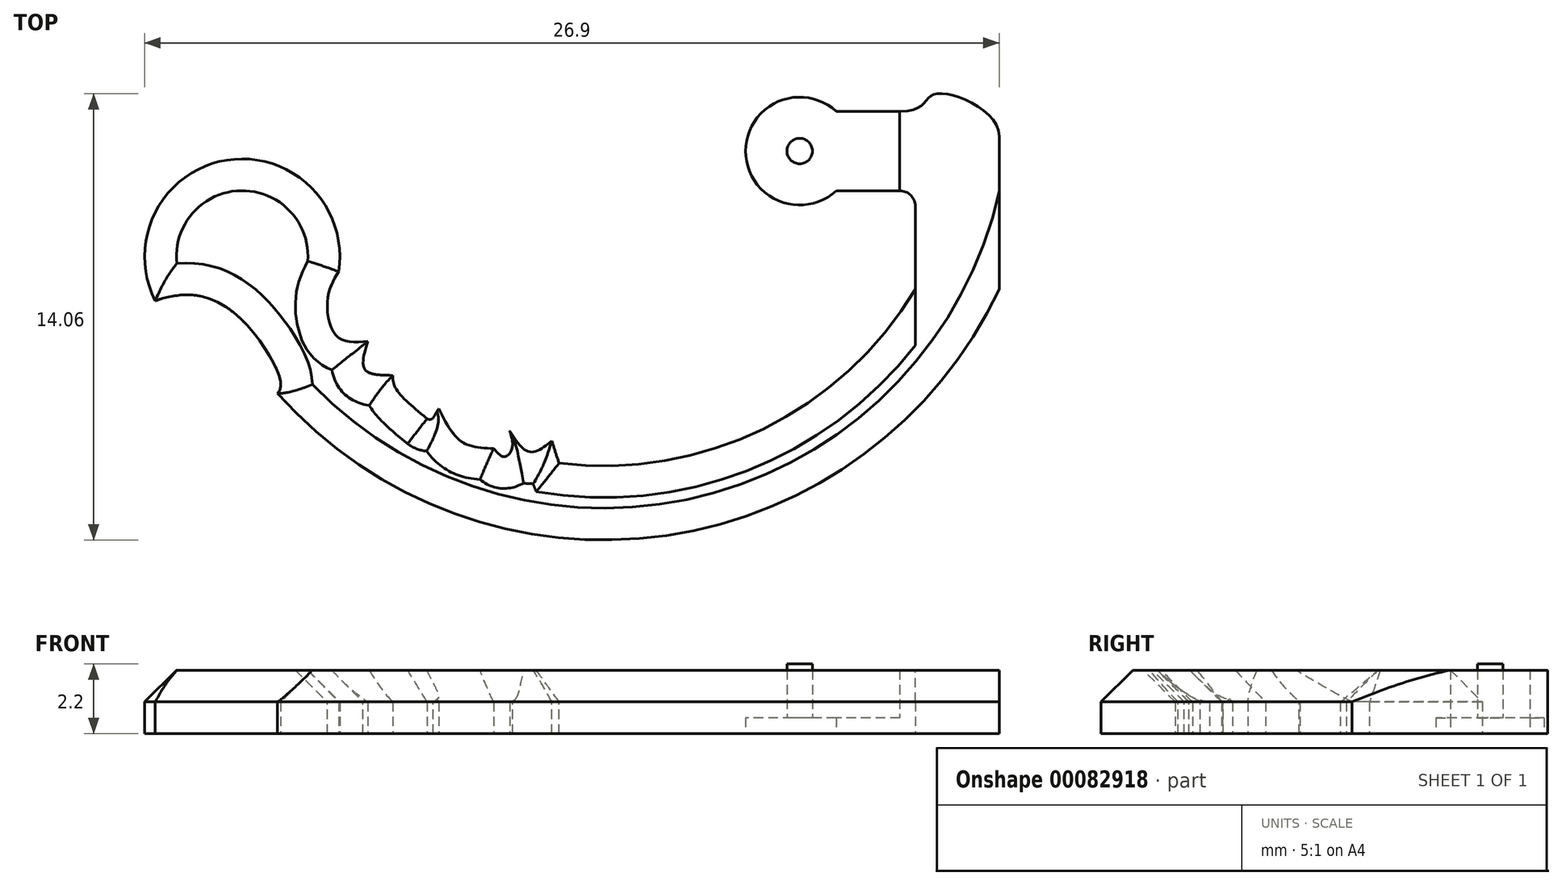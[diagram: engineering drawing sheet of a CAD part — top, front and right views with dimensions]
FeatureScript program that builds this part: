
annotation { "Feature Type Name" : "Feature", "Feature Type Description" : "" }
export const myFeature = defineFeature(function(context is Context, id is Id, definition is map)
    precondition{}
    {
        {
            var Q0;
            Q0=qCreatedBy(makeId("Top.planeOp"),FACE);
            var sketch = newSketch(context, id + "F0", { "sketchPlane" : qUnion([Q0])});
            skLineSegment(sketch, "E0.left", {"start": v(3.15, -1.25) * mm, "end": v(3.15, 1.25) * mm});
            skFitSpline(sketch, "E1", {"points": [v(3.15, 1.25) * mm, v(4.3, 1.8) * mm, v(6.28, 0.46) * mm], "startDerivative": vector(6.12, 0) * mm, "endDerivative": vector(0, -4.23) * mm});
            skLineSegment(sketch, "E2", {"start": v(6.28, 0.46) * mm, "end": v(6.28, -4.35) * mm});
            skArc(sketch, "E3", {"start": v(3.64, -1.74) * mm, "mid": v(3.5, -1.4) * mm, "end": v(3.15, -1.25) * mm});
            skLineSegment(sketch, "E4", {"start": v(3.64, -1.74) * mm, "end": v(3.64, -4.35) * mm});
            skArc(sketch, "E5", {"start": v(-16.44, -7.63) * mm, "mid": v(-4.2, -12.1) * mm, "end": v(6.28, -4.35) * mm});
            skArc(sketch, "E6.0", {"start": v(-17.2, -4.16) * mm, "mid": v(-6.56, -10.9) * mm, "end": v(4.5, -4.86) * mm});
            skFitSpline(sketch, "E7", {"points": [v(-6.56, -10.9) * mm, v(-7.28, -10.36) * mm, v(-7.8, -9.12) * mm], "startDerivative": vector(-1.76, 0.97) * mm, "endDerivative": vector(-0.75, 2.54) * mm});
            skFitSpline(sketch, "E8", {"points": [v(-7.8, -9.12) * mm, v(-8.5, -9.48) * mm, v(-9.12, -8.83) * mm], "startDerivative": vector(-1.5, -1.2) * mm, "endDerivative": vector(-1.15, 1.76) * mm});
            skFitSpline(sketch, "E9", {"points": [v(-9.63, -9.37) * mm, v(-10.63, -9.16) * mm, v(-11.36, -8.1) * mm], "startDerivative": vector(-2.3, 0.09) * mm, "endDerivative": vector(-1.18, 2.4) * mm});
            skFitSpline(sketch, "E10", {"points": [v(-11.36, -8.1) * mm, v(-11.71, -8.86) * mm, v(-11.67, -9.62) * mm], "startDerivative": vector(-0.9, -1.46) * mm, "endDerivative": vector(0.3, -1.56) * mm});
            skFitSpline(sketch, "E11", {"points": [v(-11.6, -8.53) * mm, v(-12.7, -7.48) * mm, v(-12.8, -7.06) * mm], "startDerivative": vector(-2.16, 1.75) * mm, "endDerivative": vector(-0.05, 1.12) * mm});
            skFitSpline(sketch, "E12", {"points": [v(-12.8, -7.06) * mm, v(-13.68, -6.88) * mm, v(-13.59, -5.99) * mm], "startDerivative": vector(-2.23, 0.02) * mm, "endDerivative": vector(0.67, 2.12) * mm});
            skFitSpline(sketch, "E13", {"points": [v(-12.8, -7.06) * mm, v(-13.21, -7.73) * mm, v(-13.45, -8.54) * mm], "startDerivative": vector(-0.91, -1.3) * mm, "endDerivative": vector(-0.36, -1.63) * mm});
            skFitSpline(sketch, "E14", {"points": [v(-13.59, -5.99) * mm, v(-14.56, -5.84) * mm, v(-14.85, -4.62) * mm, v(-14.51, -3.8) * mm], "startDerivative": vector(-3.43, -0.3) * mm, "endDerivative": vector(1.42, 2.32) * mm});
            skFitSpline(sketch, "E15", {"points": [v(-13.59, -5.99) * mm, v(-14.13, -6.91) * mm, v(-14.42, -7.76) * mm], "startDerivative": vector(-1.14, -1.76) * mm, "endDerivative": vector(-0.5, -1.77) * mm});
            skFitSpline(sketch, "E16", {"points": [v(-14.51, -3.8) * mm, v(-15.87, -3.46) * mm, v(-17.2, -4.16) * mm], "startDerivative": vector(-2.8, 1.18) * mm, "endDerivative": vector(-2.59, -1.88) * mm});
            skPoint(sketch, "E17", {"position": v(-16.44, -7.63) * mm});
            skPoint(sketch, "E18.orphan", {"position": v(-18.6, -4.35) * mm});
            skFitSpline(sketch, "E19", {"points": [v(-16.44, -7.63) * mm, v(-16.45, -6.91) * mm, v(-18.22, -4.8) * mm, v(-20.28, -4.71) * mm], "startDerivative": vector(2.1, 1.9) * mm, "endDerivative": vector(-5.6, -1.96) * mm});
            skArc(sketch, "E20", {"start": v(-14.51, -3.8) * mm, "mid": v(-18.03, -0.29) * mm, "end": v(-20.28, -4.71) * mm});
            skPoint(sketch, "E21", {"position": v(-7.57, -9.82) * mm});
            skArc(sketch, "E22.trimOffspring", {"start": v(-7.57, -9.82) * mm, "mid": v(-1.15, -8.75) * mm, "end": v(3.64, -4.35) * mm});
            skArc(sketch, "E23", {"start": v(6.28, -4.35) * mm, "mid": v(4.96, -3.92) * mm, "end": v(3.64, -4.35) * mm});
            skArc(sketch, "E24", {"start": v(6.28, -4.35) * mm, "mid": v(5.35, -4.45) * mm, "end": v(4.5, -4.86) * mm});
            skArc(sketch, "E25", {"start": v(3.64, -4.35) * mm, "mid": v(4.03, -4.67) * mm, "end": v(4.5, -4.86) * mm});
            skArc(sketch, "E26", {"start": v(-11.75, -8.41) * mm, "mid": v(-11.64, -8.45) * mm, "end": v(-11.53, -8.4) * mm});
            skFitSpline(sketch, "E27", {"points": [v(-9.12, -8.83) * mm, v(-9.05, -9.33) * mm, v(-9.28, -9.63) * mm, v(-9.63, -9.37) * mm], "startDerivative": vector(0.47, -1.4) * mm, "endDerivative": vector(-1.1, 1.22) * mm});
            skFitSpline(sketch, "E28", {"points": [v(-9.63, -9.37) * mm, v(-9.8, -9.82) * mm, v(-9.8, -10.37) * mm], "startDerivative": vector(-0.41, -0.9) * mm, "endDerivative": vector(0.08, -1.09) * mm});
            skSolve(sketch);
        }
        {
            var Q0;
            Q0 = qSketchRegion(id + "F0", true);
            extrude(context, id + "F1", {"entities" : qUnion([Q0]), "endBound" : BoundingType.SYMMETRIC, "depth" : 2 * mm});
        }
        {
            var Q0;
            Q0=makeQuery(id+"F1.opExtrude","CAP_EDGE",EDGE,{"disambiguationData":[OSD([sQuery(id+"F0.wireOp",EDGE,"E20")])],"isStart":false});
            var Q1;
            Q1=makeQuery(id+"F1.opExtrude","CAP_EDGE",EDGE,{"disambiguationData":[OSD([sQuery(id+"F0.wireOp",EDGE,"E14")])],"isStart":false});
            var Q2;
            Q2=makeQuery(id+"F1.opExtrude","CAP_EDGE",EDGE,{"disambiguationData":[OSD([sQuery(id+"F0.wireOp",EDGE,"E12")])],"isStart":false});
            var Q3;
            Q3=makeQuery(id+"F1.opExtrude","CAP_EDGE",EDGE,{"disambiguationData":[OSD([sQuery(id+"F0.wireOp",EDGE,"E11")])],"isStart":false});
            var Q4;
            Q4=makeQuery(id+"F1.opExtrude","CAP_EDGE",EDGE,{"disambiguationData":[OSD([sQuery(id+"F0.wireOp",EDGE,"E9")])],"isStart":false});
            var Q5;
            Q5=makeQuery(id+"F1.opExtrude","CAP_EDGE",EDGE,{"disambiguationData":[OSD([sQuery(id+"F0.wireOp",EDGE,"E10")])],"isStart":false});
            var Q6;
            Q6=makeQuery(id+"F1.opExtrude","CAP_EDGE",EDGE,{"disambiguationData":[OSD([sQuery(id+"F0.wireOp",EDGE,"E22.trimOffspring")])],"isStart":false});
            var Q7;
            Q7=makeQuery(id+"F1.opExtrude","CAP_EDGE",EDGE,{"disambiguationData":[OSD([sQuery(id+"F0.wireOp",EDGE,"E7")])],"isStart":false});
            var Q8;
            Q8=makeQuery(id+"F1.opExtrude","CAP_EDGE",EDGE,{"disambiguationData":[OSD([sQuery(id+"F0.wireOp",EDGE,"E26")])],"isStart":false});
            var Q9;
            Q9=makeQuery(id+"F1.opExtrude","CAP_EDGE",EDGE,{"disambiguationData":[OSD([sQuery(id+"F0.wireOp",EDGE,"E27")])],"isStart":false});
            var Q10;
            Q10=makeQuery(id+"F1.opExtrude","CAP_EDGE",EDGE,{"disambiguationData":[OSD([sQuery(id+"F0.wireOp",EDGE,"E8")])],"isStart":false});
            var Q11;
            Q11=makeQuery(id+"F1.opExtrude","CAP_EDGE",EDGE,{"disambiguationData":[OSD([sQuery(id+"F0.wireOp",EDGE,"E5")])],"isStart":false});
            var Q12;
            Q12=makeQuery(id+"F1.opExtrude","CAP_EDGE",EDGE,{"disambiguationData":[OSD([sQuery(id+"F0.wireOp",EDGE,"E19")])],"isStart":false});
            chamfer(context, id + "F2", {"entities" : qUnion([Q0, Q1, Q2, Q3, Q4, Q5, Q6, Q7, Q8, Q9, Q10, Q11, Q12]), "width" : 1 * mm, "tangentPropagation" : true});
        }
        {
            var Q0;
            Q0=qCreatedBy(makeId("Top.planeOp"),FACE);
            var sketch = newSketch(context, id + "F3", { "sketchPlane" : qUnion([Q0])});
            skLineSegment(sketch, "E29.bottom", {"start": v(3.15, 1.25) * mm, "end": v(1.15, 1.25) * mm});
            skLineSegment(sketch, "E29.top", {"start": v(3.15, -1.25) * mm, "end": v(1.15, -1.25) * mm});
            skLineSegment(sketch, "E29.left", {"start": v(3.15, 1.25) * mm, "end": v(3.15, -1.25) * mm});
            skLineSegment(sketch, "E29.right", {"start": v(1.15, 1.25) * mm, "end": v(1.15, -1.25) * mm});
            skCircle(sketch, "E30", {"center": v(0, 0) * mm, "radius": 1.7 * mm});
            skCircle(sketch, "E31", {"center": v(0, 0) * mm, "radius": 0.4 * mm});
            skSolve(sketch);
        }
        {
            var Q0;
            Q0=makeQuery(id+"F3.imprint","IMPRINT",FACE,{"disambiguationData":[TD([[makeQuery(id+"F3.imprint","IMPRINT",EDGE,{"derivedFrom":sQuery(id+"F3.wireOp",EDGE,"E31")}),1.0]])]});
            var Q1;
            {var subQ0=sQuery(id+"F3.wireOp",EDGE,"E29.right");Q1=makeQuery(id+"F3.imprint","IMPRINT",FACE,{"disambiguationData":[TD([[makeQuery(id+"F3.imprint","IMPRINT",EDGE,{"derivedFrom":subQ0}),-1.0]])]});}
            var Q2;
            {var subQ0=sQuery(id+"F3.wireOp",EDGE,"E29.bottom");Q2=makeQuery(id+"F3.imprint","IMPRINT",FACE,{"disambiguationData":[TD([[makeQuery(id+"F3.imprint","IMPRINT",EDGE,{"derivedFrom":subQ0}),1.0]])]});}
            var Q3;
            {var subQ0=sQuery(id+"F3.wireOp",EDGE,"E29.right");Q3=makeQuery(id+"F3.imprint","IMPRINT",FACE,{"disambiguationData":[TD([[makeQuery(id+"F3.imprint","IMPRINT",EDGE,{"derivedFrom":subQ0}),1.0]])]});}
            extrude(context, id + "F4", {"entities" : qUnion([Q0, Q1, Q2, Q3]), "operationType" : NewBodyOperationType.ADD, "depth" : 1.2 * mm, "hasSecondDirection" : true, "secondDirectionOppositeDirection" : true, "secondDirectionDepth" : 1 * mm});
        }
        {
            var Q0;
            Q0 = qSketchRegion(id + "F3", true);
            extrude(context, id + "F5", {"entities" : qUnion([Q0]), "operationType" : NewBodyOperationType.REMOVE, "depth" : 1.7 * mm, "hasSecondDirection" : true, "secondDirectionOppositeDirection" : true, "secondDirectionDepth" : 0.5 * mm});
        }
    });
